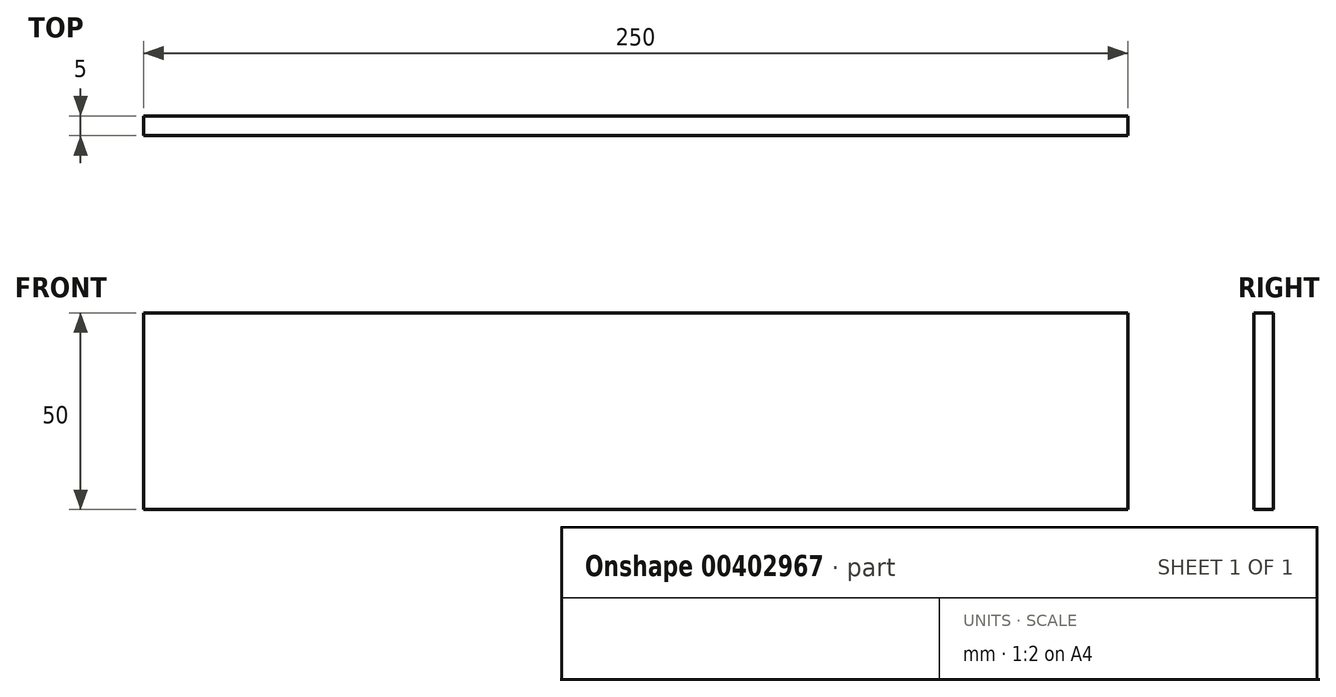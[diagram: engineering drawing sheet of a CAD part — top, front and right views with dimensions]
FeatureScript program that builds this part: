
annotation { "Feature Type Name" : "Feature", "Feature Type Description" : "" }
export const myFeature = defineFeature(function(context is Context, id is Id, definition is map)
    precondition{}
    {
        {
            var Q0;
            Q0=qCreatedBy(makeId("Right.planeOp"),FACE);
            var sketch = newSketch(context, id + "F0", { "sketchPlane" : qUnion([Q0])});
            skLineSegment(sketch, "E0.bottom", {"start": v(2.5, 25) * mm, "end": v(-2.5, 25) * mm});
            skLineSegment(sketch, "E0.top", {"start": v(2.5, -25) * mm, "end": v(-2.5, -25) * mm});
            skLineSegment(sketch, "E0.left", {"start": v(2.5, 25) * mm, "end": v(2.5, -25) * mm});
            skLineSegment(sketch, "E0.right", {"start": v(-2.5, 25) * mm, "end": v(-2.5, -25) * mm});
            skPoint(sketch, "E0.middle", {"position": v(0, 0) * mm});
            skSolve(sketch);
        }
        {
            var Q0;
            Q0 = qSketchRegion(id + "F0", true);
            extrude(context, id + "F1", {"entities" : qUnion([Q0]), "endBound" : BoundingType.SYMMETRIC, "depth" : 250 * mm});
        }
    });
